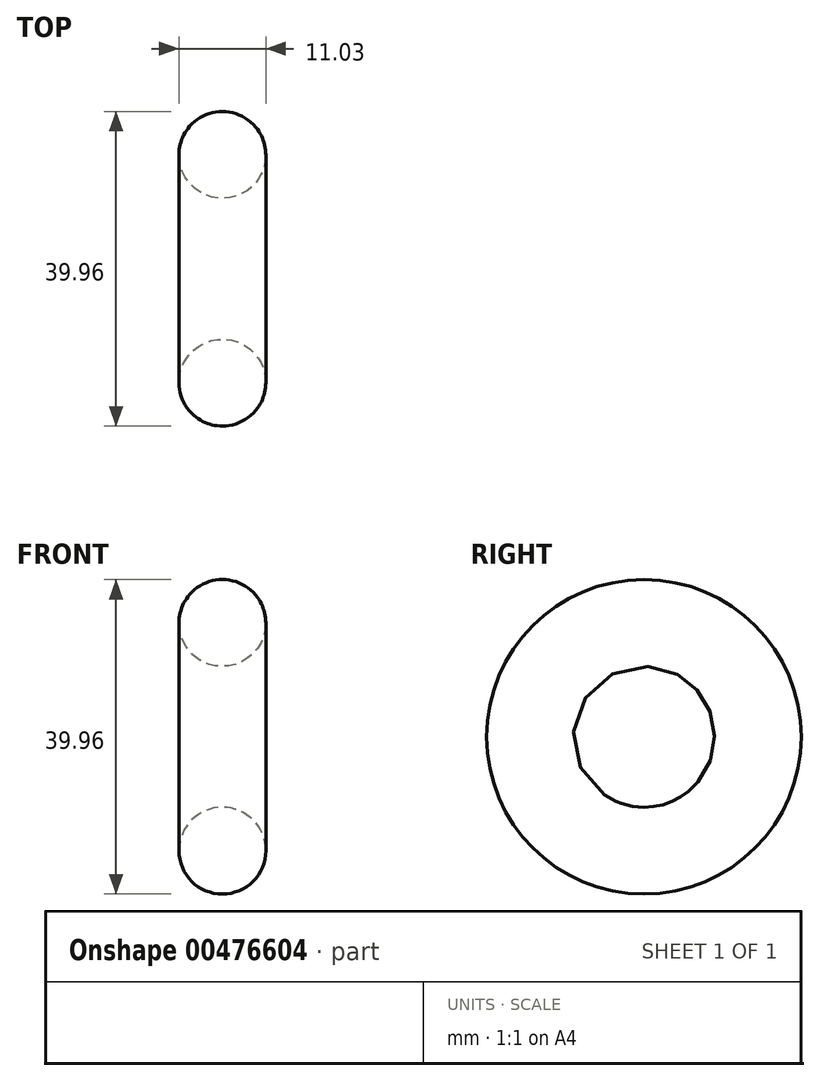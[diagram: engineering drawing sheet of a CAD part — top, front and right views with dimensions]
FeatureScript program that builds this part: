
annotation { "Feature Type Name" : "Feature", "Feature Type Description" : "" }
export const myFeature = defineFeature(function(context is Context, id is Id, definition is map)
    precondition{}
    {
        {
            var Q0;
            Q0=qCreatedBy(makeId("Front.planeOp"),FACE);
            var sketch = newSketch(context, id + "F0", { "sketchPlane" : qUnion([Q0])});
            skCircle(sketch, "E0", {"center": v(-49.91, 64.78) * mm, "radius": 5.51 * mm});
            skSolve(sketch);
        }
        {
            var Q0;
            Q0=qCreatedBy(makeId("Front.planeOp"),FACE);
            var sketch = newSketch(context, id + "F1", { "sketchPlane" : qUnion([Q0])});
            skLineSegment(sketch, "E1", {"start": v(-31.68, 50.31) * mm, "end": v(-68.67, 50.31) * mm, "construction": true});
            skSolve(sketch);
        }
        {
            var Q0;
            Q0=makeQuery(id+"F0.imprint","IMPRINT",FACE,{"disambiguationData":[TD([[makeQuery(id+"F0.imprint","IMPRINT",EDGE,{"derivedFrom":sQuery(id+"F0.wireOp",EDGE,"E0")}),1.0]])]});
            var Q1;
            Q1=sQuery(id+"F1.wireOp",EDGE,"E1");
            revolve(context, id + "F2", {"entities" : qUnion([Q0]), "axis" : qUnion([Q1]), "revolveType" : RevolveType.FULL});
        }
        {
            var Q0;
            Q0=qCreatedBy(makeId("Front.planeOp"),FACE);
            var sketch = newSketch(context, id + "F3", { "sketchPlane" : qUnion([Q0])});
            skLineSegment(sketch, "E2", {"start": v(-25.8, 24.88) * mm, "end": v(-72.3, 24.88) * mm, "construction": true});
            skSolve(sketch);
        }
    });
